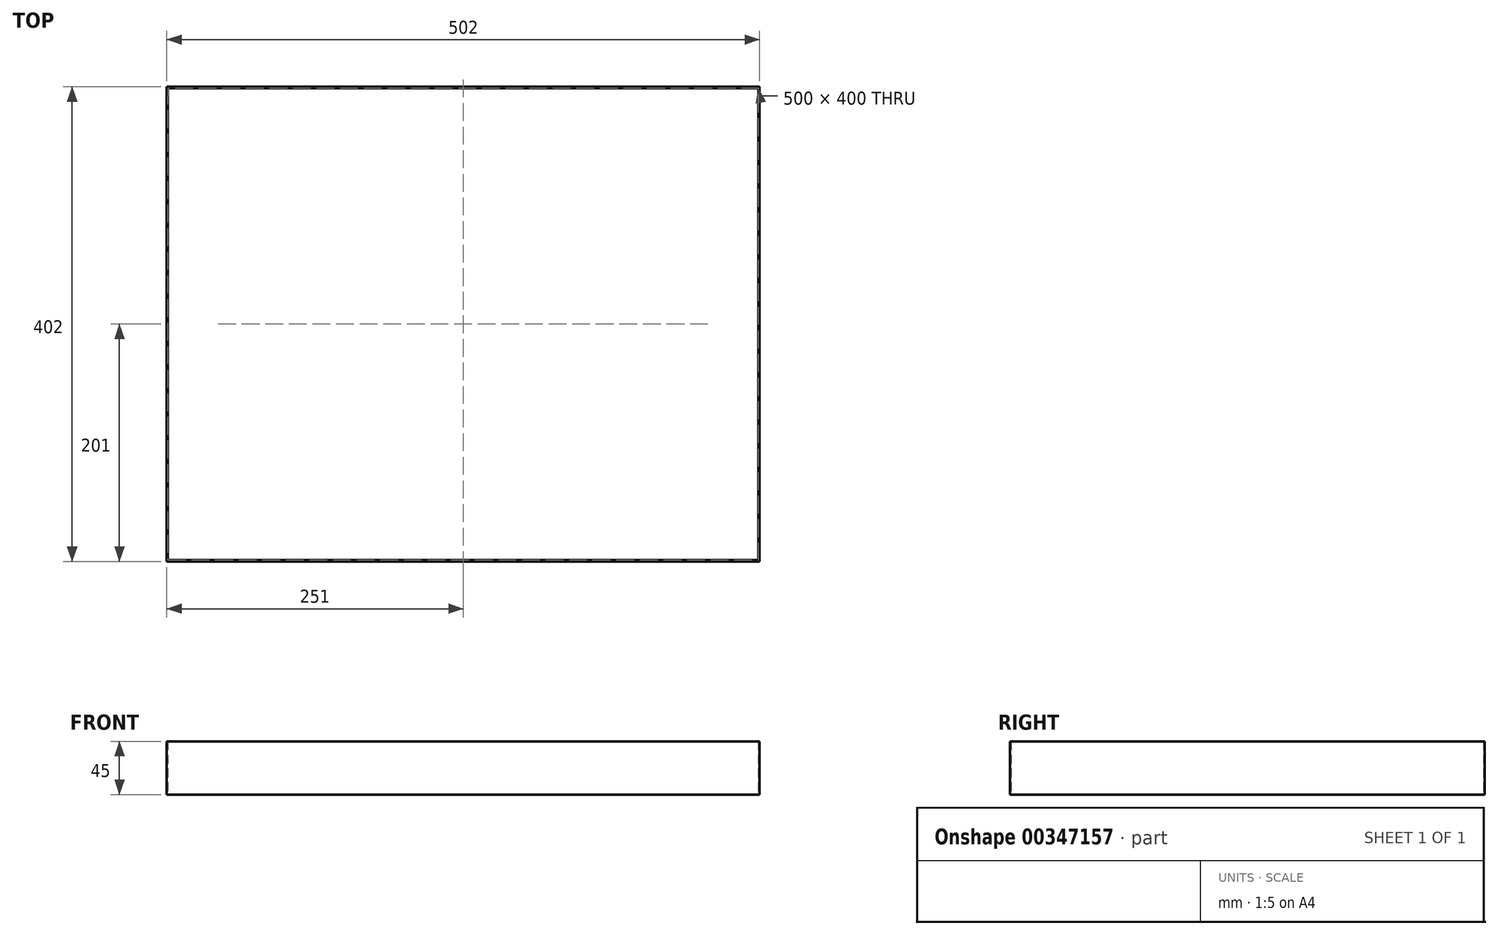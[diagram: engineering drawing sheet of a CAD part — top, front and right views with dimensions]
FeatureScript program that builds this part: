
annotation { "Feature Type Name" : "Feature", "Feature Type Description" : "" }
export const myFeature = defineFeature(function(context is Context, id is Id, definition is map)
    precondition{}
    {
        {
            var Q0;
            Q0=qCreatedBy(makeId("Top.planeOp"),FACE);
            var sketch = newSketch(context, id + "F0", { "sketchPlane" : qUnion([Q0])});
            skLineSegment(sketch, "E0.bottom", {"start": v(250, 200) * mm, "end": v(-250, 200) * mm});
            skLineSegment(sketch, "E0.top", {"start": v(250, -200) * mm, "end": v(-250, -200) * mm});
            skLineSegment(sketch, "E0.left", {"start": v(250, 200) * mm, "end": v(250, -200) * mm});
            skLineSegment(sketch, "E0.right", {"start": v(-250, 200) * mm, "end": v(-250, -200) * mm});
            skPoint(sketch, "E0.middle", {"position": v(0, 0) * mm});
            skLineSegment(sketch, "E1.0", {"start": v(251, 201) * mm, "end": v(-251, 201) * mm});
            skLineSegment(sketch, "E1.1", {"start": v(251, 201) * mm, "end": v(251, -201) * mm});
            skLineSegment(sketch, "E1.2", {"start": v(251, -201) * mm, "end": v(-251, -201) * mm});
            skLineSegment(sketch, "E1.3", {"start": v(-251, 201) * mm, "end": v(-251, -201) * mm});
            skSolve(sketch);
        }
        {
            var Q0;
            Q0=makeQuery(id+"F0.imprint","IMPRINT",FACE,{"disambiguationData":[TD([[makeQuery(id+"F0.imprint","IMPRINT",EDGE,{"derivedFrom":sQuery(id+"F0.wireOp",EDGE,"E0.bottom")}),-1.0]])]});
            extrude(context, id + "F1", {"entities" : qUnion([Q0]), "depth" : 45 * mm, "offsetDistance" : 25 * mm});
        }
    });
